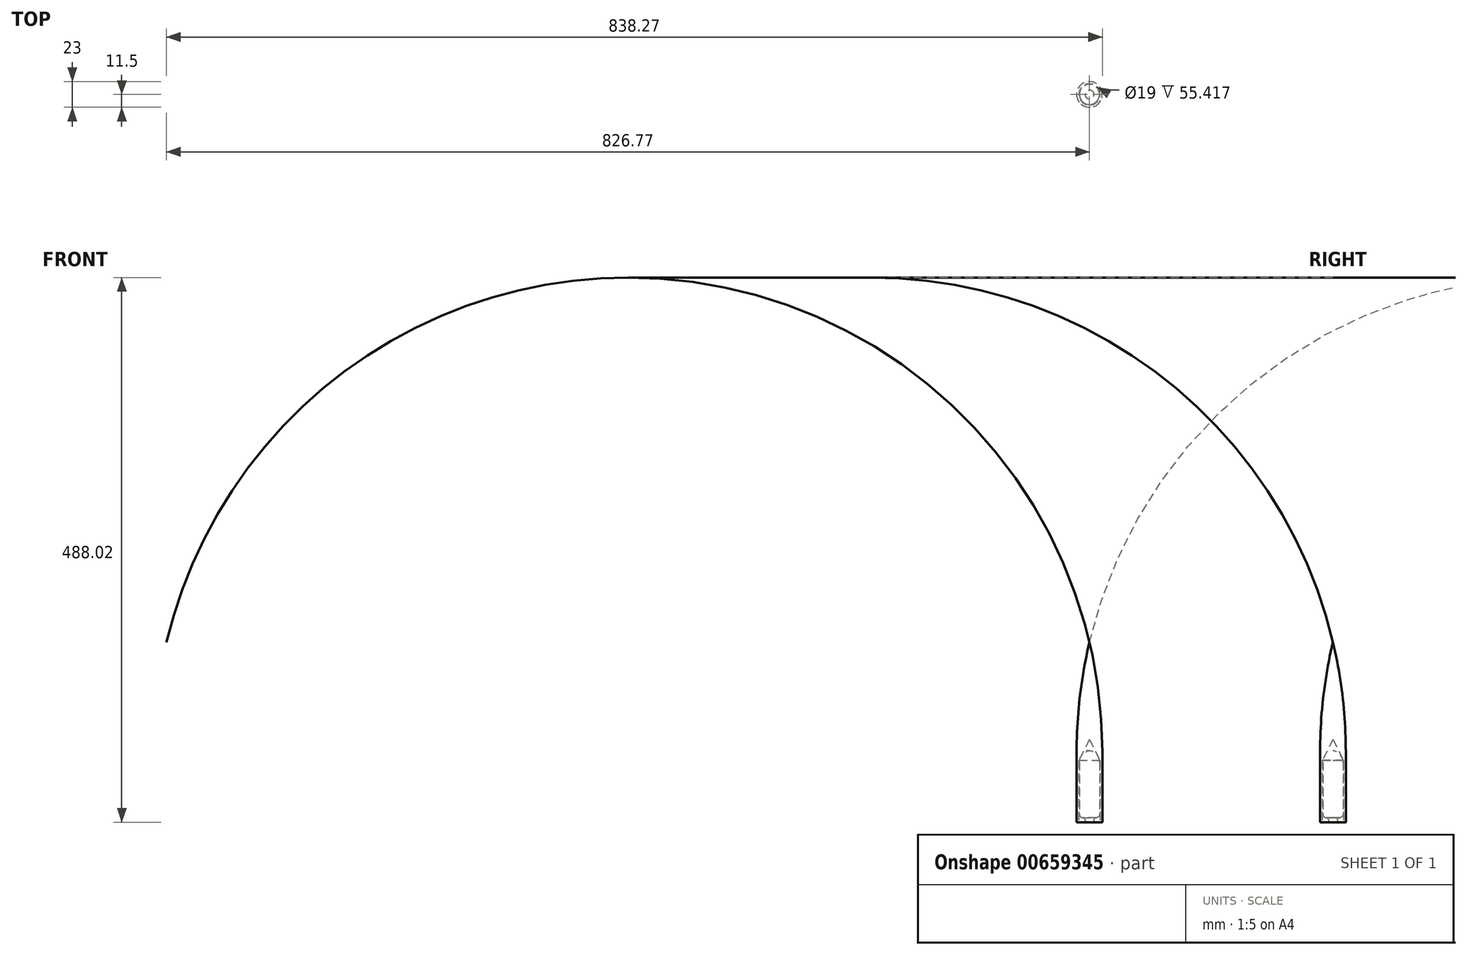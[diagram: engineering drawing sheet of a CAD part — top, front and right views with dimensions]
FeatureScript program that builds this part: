
annotation { "Feature Type Name" : "Feature", "Feature Type Description" : "" }
export const myFeature = defineFeature(function(context is Context, id is Id, definition is map)
    precondition{}
    {
        {
            var Q0;
            Q0=qCreatedBy(makeId("Right.planeOp"),FACE);
            var sketch = newSketch(context, id + "F0", { "sketchPlane" : qUnion([Q0])});
            skLineSegment(sketch, "E0", {"start": v(0, 0) * mm, "end": v(0, 64) * mm});
            skLineSegment(sketch, "E1", {"start": v(0, 0) * mm, "end": v(4, 0) * mm});
            skLineSegment(sketch, "E2", {"start": v(9, 53.67) * mm, "end": v(9, 6.94) * mm});
            skArc(sketch, "E3", {"start": v(6.1, 4.1) * mm, "mid": v(8.15, 4.9) * mm, "end": v(9, 6.94) * mm});
            skArc(sketch, "E4", {"start": v(6.1, 4.1) * mm, "mid": v(4.62, 3.52) * mm, "end": v(4, 2.05) * mm});
            skLineSegment(sketch, "E5", {"start": v(4, 0) * mm, "end": v(4, 2.05) * mm});
            skArc(sketch, "E6", {"start": v(9, 53.67) * mm, "mid": v(6.43, 60.52) * mm, "end": v(0, 64) * mm});
            skSolve(sketch);
        }
        {
            var Q0;
            Q0 = qSketchRegion(id + "F0", true);
            var Q1;
            Q1=sQuery(id+"F0.wireOp",EDGE,"E0");
            revolve(context, id + "F1", {"surfaceOperationType" : NewSurfaceOperationType.NEW, "entities" : qUnion([Q0]), "axis" : qUnion([Q1]), "revolveType" : RevolveType.FULL});
        }
        {
            var Q0;
            Q0=qCreatedBy(makeId("Right.planeOp"),FACE);
            var sketch = newSketch(context, id + "F2", { "sketchPlane" : qUnion([Q0])});
            skLineSegment(sketch, "E7", {"start": v(0, 0) * mm, "end": v(0, 161.32) * mm});
            skLineSegment(sketch, "E8", {"start": v(0, 74.08) * mm, "end": v(9.5, 55.42) * mm});
            skLineSegment(sketch, "E9", {"start": v(9.5, 55.42) * mm, "end": v(9.5, 0) * mm});
            skLineSegment(sketch, "E10", {"start": v(9.5, 0) * mm, "end": v(11.5, 0) * mm});
            skLineSegment(sketch, "E11", {"start": v(11.5, 0) * mm, "end": v(11.5, 63.14) * mm});
            skArc(sketch, "E12", {"start": v(11.5, 63.14) * mm, "mid": v(8.62, 112.57) * mm, "end": v(0, 161.32) * mm});
            skSolve(sketch);
        }
        {
            var Q0;
            Q0 = qSketchRegion(id + "F2", true);
            var Q1;
            Q1=sQuery(id+"F2.wireOp",EDGE,"E7");
            revolve(context, id + "F3", {"entities" : qUnion([Q0]), "axis" : qUnion([Q1]), "revolveType" : RevolveType.FULL});
        }
    });
